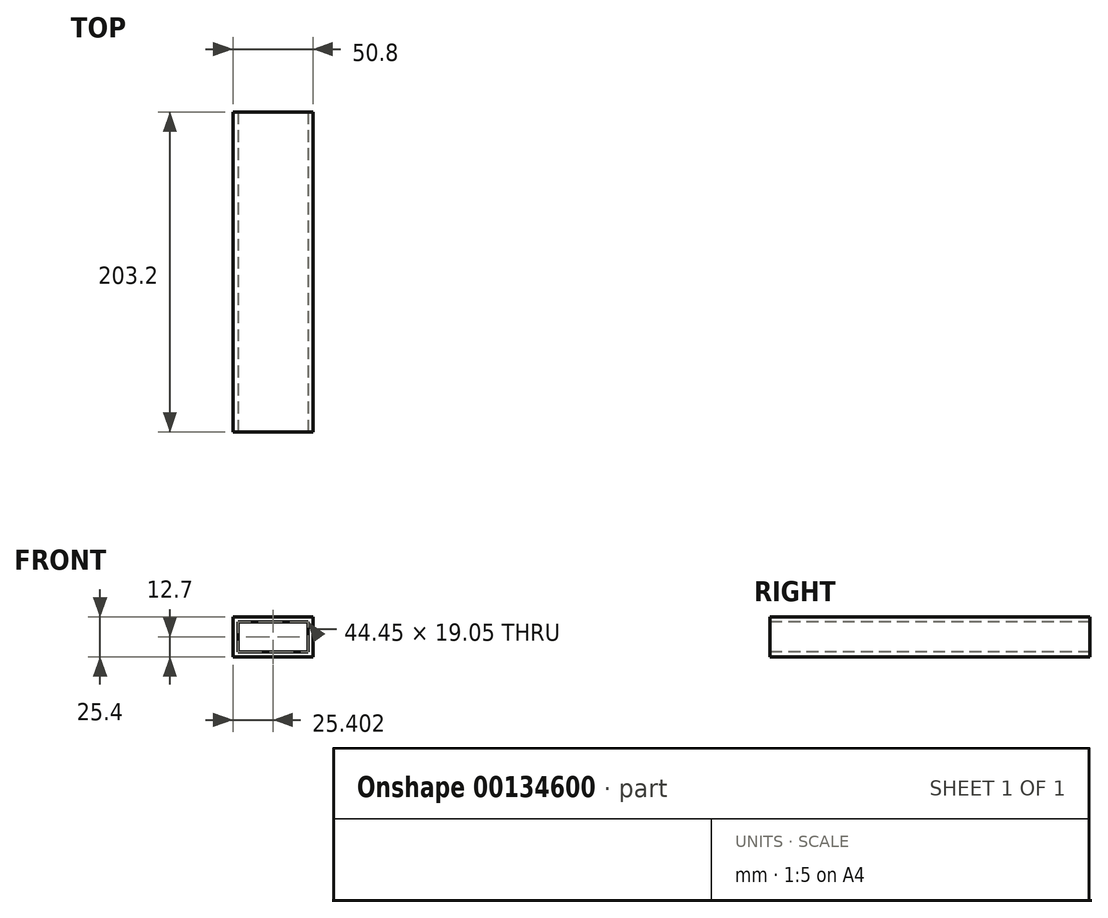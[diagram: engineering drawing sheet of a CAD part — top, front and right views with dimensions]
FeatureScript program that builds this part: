
annotation { "Feature Type Name" : "Feature", "Feature Type Description" : "" }
export const myFeature = defineFeature(function(context is Context, id is Id, definition is map)
    precondition{}
    {
        {
            var Q0;
            Q0=qCreatedBy(makeId("Top.planeOp"),FACE);
            var sketch = newSketch(context, id + "F0", { "sketchPlane" : qUnion([Q0])});
            skLineSegment(sketch, "E0.bottom", {"start": v(-59.12, 94.16) * mm, "end": v(-8.32, 94.16) * mm});
            skLineSegment(sketch, "E0.top", {"start": v(-59.12, -109.04) * mm, "end": v(-8.32, -109.04) * mm});
            skLineSegment(sketch, "E0.left", {"start": v(-59.12, 94.16) * mm, "end": v(-59.12, -109.04) * mm});
            skLineSegment(sketch, "E0.right", {"start": v(-8.32, 94.16) * mm, "end": v(-8.32, -109.04) * mm});
            skSolve(sketch);
        }
        {
            var Q0;
            Q0 = qSketchRegion(id + "F0", true);
            extrude(context, id + "F1", {"entities" : qUnion([Q0]), "depth" : 25.4 * mm});
        }
        {
            var Q0;
            Q0=makeQuery(id+"F1.opExtrude","SWEPT_FACE",FACE,{"disambiguationData":[OSD([sQuery(id+"F0.wireOp",EDGE,"E0.bottom")])]});
            var Q1;
            Q1=makeQuery(id+"F1.opExtrude","SWEPT_FACE",FACE,{"disambiguationData":[OSD([sQuery(id+"F0.wireOp",EDGE,"E0.top")])]});
            shell(context, id + "F2", {"entities" : qUnion([Q0, Q1]), "thickness" : 3.17 * mm});
        }
    });
